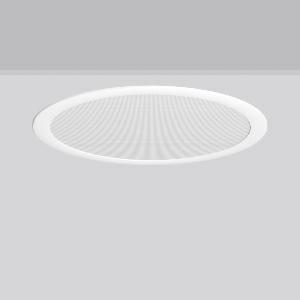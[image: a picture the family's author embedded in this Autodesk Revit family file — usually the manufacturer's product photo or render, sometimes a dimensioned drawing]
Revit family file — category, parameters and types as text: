
# Revit family: toledo_flat_round_e_901586_002_1_0fdf
name_source: partatom
category: Lighting Fixtures
units: mm (PartAtom-declared; Revit-internal decimal feet)

## family parameters
Cut with Voids When Loaded = No
Host = Face
Light Source = No
Part Type = Normal
Room Calculation Point = No
Round Connector Dimension = Use Diameter
Shared = No

## types (1)
- TOLEDO FLAT round E (1 x LED Modul 840, 3550 lm, 4000)
    Apparent Load = 30 VA
    CIE Flux Codes = 60 86 96 100 100
    Color Rendering = 80
    Color Temperature = 4000
    Default Elevation = 1800 mm
    Description = Series: TOLEDO FLAT round
Ultra thin recessed downlight. Housing: die-cast aluminium. Lightguide and diffuser made of non-yellowing PMMA, prismatic. Ceiling installation with spring system. Mounting depth depends on ceiling strength. Including separate LED converter with connecting cable 250 mm. Suitable for through-wiring with separately available accessories. Surface mounted housing as accessory for all sizes. Retrofittable decorative cylinders made of chintz fabric as accessory, optional with satin finish plastic diffuser. Through-wiring box (5 pole) available as accessory. 
Colour: white
Diameter: 495 mm
Height: 6 mm
Cut-out diameter: 470 mm
Recess height: 40-59 mm
Luminaire: recess height: 31-51 mm
Lamp: LED
Socket: without socket
Colour temperature: 4000K
Colour rendering index (CRI): 80
System power: 30 W
Rated luminous flux: 3550 lm
Luminous efficiency: 118 lm/W
Control gear: Regulated power supply
Protection class: II
Type of protection: IP 54
    Height = 0 mm  [stored 0 ft]
    Lamp = 1 x LED Modul 840
    Lamp Light Flux = 3550 lm
    Lamp count = 1
    Length = 495 mm
    Lifetime = 50000 h
    Luminous efficacy = 118 lm/W
    Manufacturer = RZB
    ModVariant = No
    Model = 901586.002.1
    Mounting Place = Ceiling
    Mounting Type = Recessed
    Number of Poles = 1
    OnlyDefault = Yes
    Power Factor = 1
    Product Name = TOLEDO FLAT round E
    Product group = Recessed downlights
    ProductGroupID = 402
    Protection Class = Protection class II
    Protection Degree = IP 20
    RLX_Detail_Level = 1
    RLX_Emergency_Light_Flux = 0 lm
    RLX_Emergency_Type = 0
    RLX_Emergency_Type_DB = No
    RlxData = <blob elided: 38477 chars, md5=7382f214>
    Socket = socket
    Standby Power = 0 W
    System Light Flux = 3550 lm
    System Power = 30 W
    Type Comments = Product without accessories
    Type Image = 901586.002.jpg
    URL = http://relux.com
    VarID = ---
    Voltage = 230 V
    Voltage Range = 220-240 V
    Weight = 0.00 kg
    Width = 0 mm  [stored 0 ft]

note: [stored X ft] marks values corroborated as IEEE doubles in the binary element streams (Revit-internal decimal feet)

## geometry (parser evidence)
native form markers: Blend x4, Sweep x10
no freeform markers — native parametric forms only
